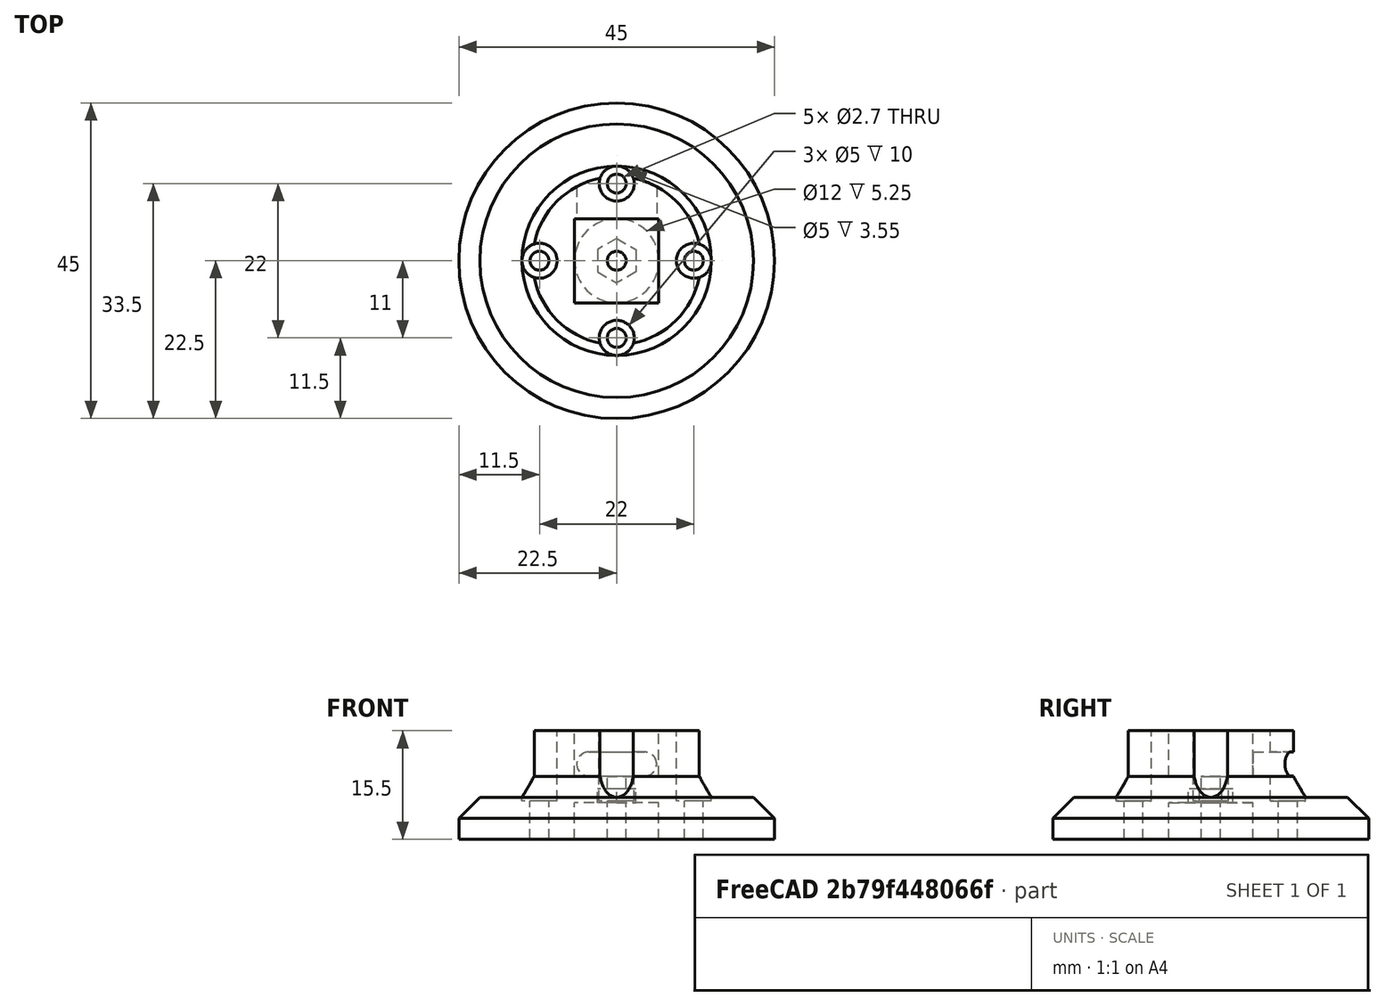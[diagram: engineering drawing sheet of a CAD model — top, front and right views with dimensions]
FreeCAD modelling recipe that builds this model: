
FCSTD DOCUMENT  (FreeCAD 0.14R2935 (Git))
Label: tendon_wheel_mx_12_23_mm
License: CC-BY 3.0
LicenseURL: http://creativecommons.org/licenses/by/3.0/
objects: Part::Cylinder×14, Part::MultiFuse×5, Part::Cut×3, Part::Box×2, Part::Cone×1, Part::Extrusion×1, Part::Mirroring×1, Part::Chamfer×1
note: 28 computed .brp shape members not serialized (recipe doc carries the construction recipe); baked Part::Feature solids carry a one-line shape summary decoded from their .brp

FEATURE [Part::Cylinder] Cylinder
  Angle = 360
  Height = 6
  Placement = pos=(0,0,-1) rot=(0,0,1;0rad)
  Radius = 22.5
FEATURE [Part::Cone] Cone
  Angle = 360
  Height = 4
  Placement = pos=(0,0,4) rot=(0,0,1;0rad)
  Radius1 = 14
  Radius2 = 12
FEATURE [Part::Cylinder] Cylinder001
  Angle = 360
  Height = 6.5
  Placement = pos=(0,0,8) rot=(0,0,1;0rad)
  Radius = 12
FEATURE [Part::MultiFuse] Fusion
  Shapes = -> [Cylinder,Cylinder001,Cone]
FEATURE [Part::Cylinder] Cylinder003  label="TopHole003"
  Angle = 360
  Height = 20
  Placement = pos=(-11,0,-3) rot=(0,0,1;0rad)
  Radius = 1.35
FEATURE [Part::Cylinder] Cylinder004  label="TopHole002"
  Angle = 360
  Height = 20
  Placement = pos=(0,-11,-3) rot=(0,0,1;0rad)
  Radius = 1.35
FEATURE [Part::Cylinder] Cylinder005  label="TopHole001"
  Angle = 360
  Height = 20
  Placement = pos=(11,0,-3) rot=(0,0,1;0rad)
  Radius = 1.35
FEATURE [Part::Cylinder] Cylinder006  label="TopHole"
  Angle = 360
  Height = 10
  Placement = pos=(0,11,-3) rot=(0,0,1;0rad)
  Radius = 1.35
FEATURE [Part::Cylinder] Cylinder007  label="TopHole004"
  Angle = 360
  Height = 20
  Placement = pos=(-11,0,2.5) rot=(0,0,1;0rad)
  Radius = 2.5
FEATURE [Part::Cylinder] Cylinder008  label="TopHole005"
  Angle = 360
  Height = 20
  Placement = pos=(11,0,2.5) rot=(0,0,1;0rad)
  Radius = 2.5
FEATURE [Part::Cylinder] Cylinder009  label="TopHole006"
  Angle = 360
  Height = 20
  Placement = pos=(0,11,2.5) rot=(0,0,1;0rad)
  Radius = 2.5
FEATURE [Part::Cylinder] Cylinder010  label="TopHole007"
  Angle = 360
  Height = 20
  Placement = pos=(0,-11,2.5) rot=(0,0,1;0rad)
  Radius = 2.5
FEATURE [Part::MultiFuse] Fusion001
  Placement = pos=(0,0,2) rot=(0,0,1;0rad)
  Shapes = -> [Cylinder010,Cylinder007,Cylinder005,Cylinder003,Cylinder009,Cylinder004,Cylinder008,Cylinder006]
FEATURE [Part::Cylinder] Cylinder012  label="Cylinder003"
  Angle = 360
  Height = 10
  Placement = pos=(-4,13,9.75) rot=(1,0,0;1.5708rad)
  Radius = 1.7
FEATURE [Part::Cylinder] Cylinder013  label="Cylinder004"
  Angle = 360
  Height = 20
  Placement = pos=(0,0,-5) rot=(0,0,1;0rad)
  Radius = 1.35
FEATURE [Part::Box] Box  label="Cube"
  Height = 8
  Length = 12
  Placement = pos=(-6,-6,8) rot=(0,0,1;0rad)
  Width = 12
FEATURE [Part::Extrusion] Extrude
  Dir = (0,0,2)
  Solid = true
FEATURE [Part::Mirroring] Part__Mirroring  label="Extrude (Mirror #1)"
  Base = (0,0,0)
  Normal = (1,0,0)
  Source = -> Extrude
FEATURE [Part::MultiFuse] Fusion002
  Placement = pos=(0,0,4.2) rot=(0,0,1;0rad)
  Shapes = -> [Part__Mirroring,Extrude]
FEATURE [Part::MultiFuse] Fusion003
  Shapes = -> [Fusion002,Fusion001,Cylinder012,Box,Cylinder013]
FEATURE [Part::Cut] Cut
  Base = -> Fusion
  Tool = -> Fusion003
FEATURE [Part::Cylinder] Cylinder014  label="Cylinder005"
  Angle = 360
  Height = 6
  Placement = pos=(0,0,-1.75) rot=(0,0,1;0rad)
  Radius = 6
FEATURE [Part::Cut] Cut001
  Base = -> Cut
  Tool = -> Cylinder014
FEATURE [Part::Cylinder] Cylinder015  label="Cylinder006"
  Angle = 360
  Height = 10
  Placement = pos=(4,15,9.75) rot=(1,0,0;1.5708rad)
  Radius = 1.7
FEATURE [Part::Box] Box001  label="Cube001"
  Height = 3.4
  Length = 8
  Placement = pos=(-4,5,8.05) rot=(0,0,1;0rad)
  Width = 8
FEATURE [Part::MultiFuse] Fusion004
  Shapes = -> [Cylinder015,Box001]
FEATURE [Part::Cut] Cut002
  Base = -> Cut001
  Tool = -> Fusion004
FEATURE [Part::Chamfer] Chamfer
  Base = -> Cut002
  Edges = 1 edges r=3: [Edge1]
